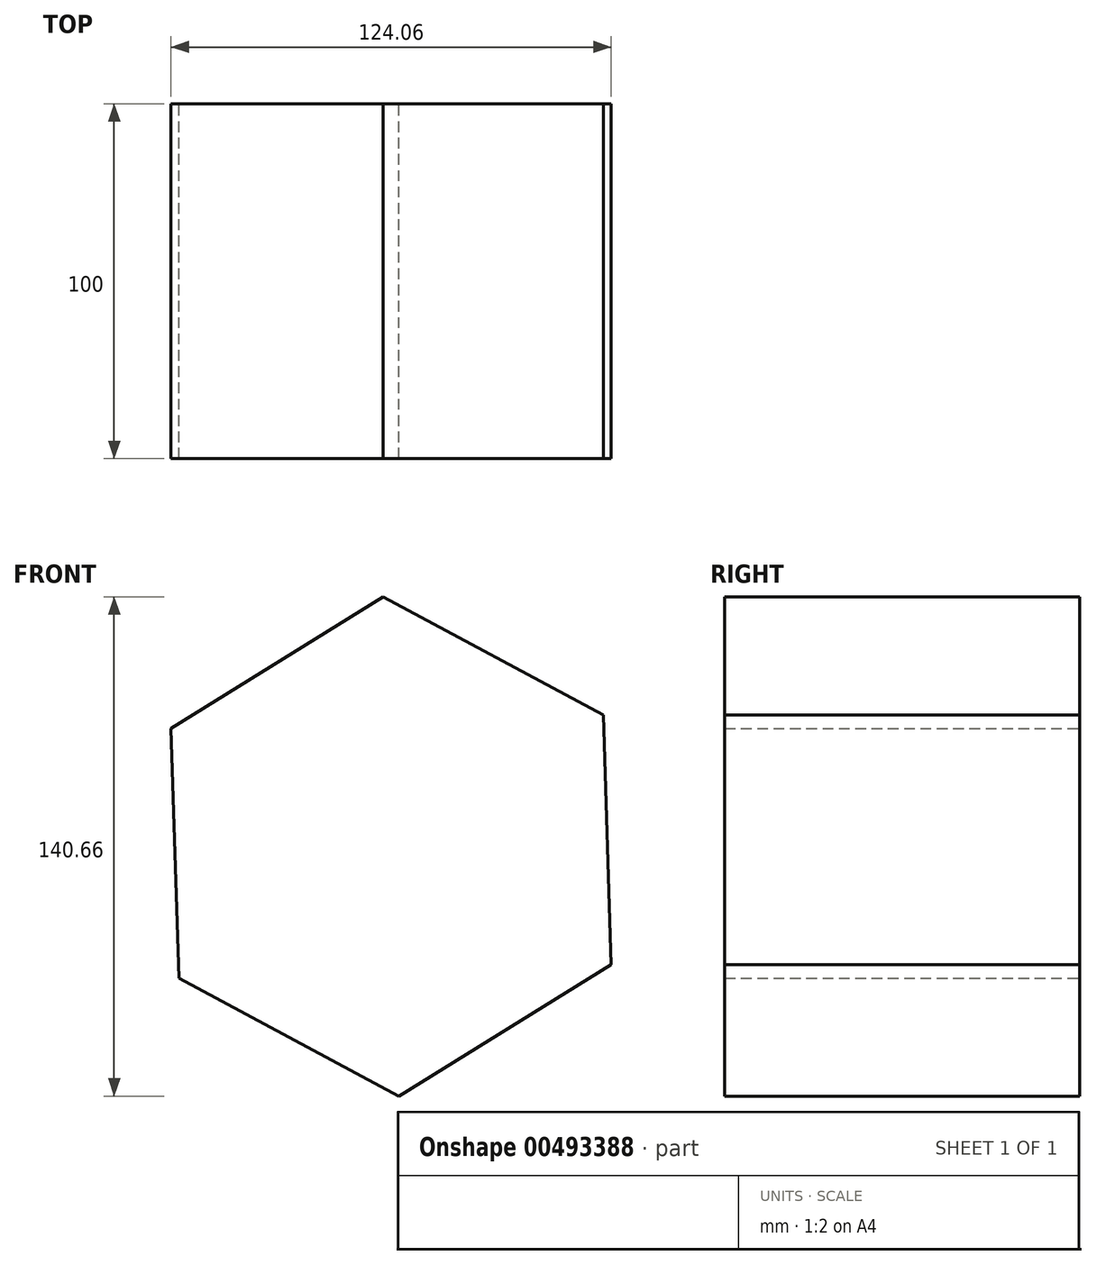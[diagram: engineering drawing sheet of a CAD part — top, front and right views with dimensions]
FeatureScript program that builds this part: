
annotation { "Feature Type Name" : "Feature", "Feature Type Description" : "" }
export const myFeature = defineFeature(function(context is Context, id is Id, definition is map)
    precondition{}
    {
        {
            var Q0;
            Q0=qCreatedBy(makeId("Front.planeOp"),FACE);
            var sketch = newSketch(context, id + "F0", { "sketchPlane" : qUnion([Q0])});
            skCircle(sketch, "E0.cCircle", {"center": v(0, 0) * mm, "radius": 60.94 * mm, "construction": true});
            skLineSegment(sketch, "E0.0", {"start": v(-62.03, 33.23) * mm, "end": v(-2.23, 70.33) * mm});
            skLineSegment(sketch, "E0.1", {"start": v(-2.23, 70.33) * mm, "end": v(59.8, 37.1) * mm});
            skLineSegment(sketch, "E0.2", {"start": v(59.8, 37.1) * mm, "end": v(62.03, -33.23) * mm});
            skLineSegment(sketch, "E0.3", {"start": v(62.03, -33.23) * mm, "end": v(2.23, -70.33) * mm});
            skLineSegment(sketch, "E0.4", {"start": v(2.23, -70.33) * mm, "end": v(-59.8, -37.1) * mm});
            skLineSegment(sketch, "E0.5", {"start": v(-59.8, -37.1) * mm, "end": v(-62.03, 33.23) * mm});
            skPoint(sketch, "E0.0.midPoint", {"position": v(-32.13, 51.78) * mm});
            skSolve(sketch);
        }
        {
            var Q0;
            Q0=makeQuery(id+"F0.imprint","IMPRINT",FACE,{"disambiguationData":[TD([[makeQuery(id+"F0.imprint","IMPRINT",EDGE,{"derivedFrom":sQuery(id+"F0.wireOp",EDGE,"E0.0")}),-1.0]])]});
            extrude(context, id + "F1", {"entities" : qUnion([Q0]), "endBound" : BoundingType.SYMMETRIC, "depth" : 100 * mm});
        }
    });
